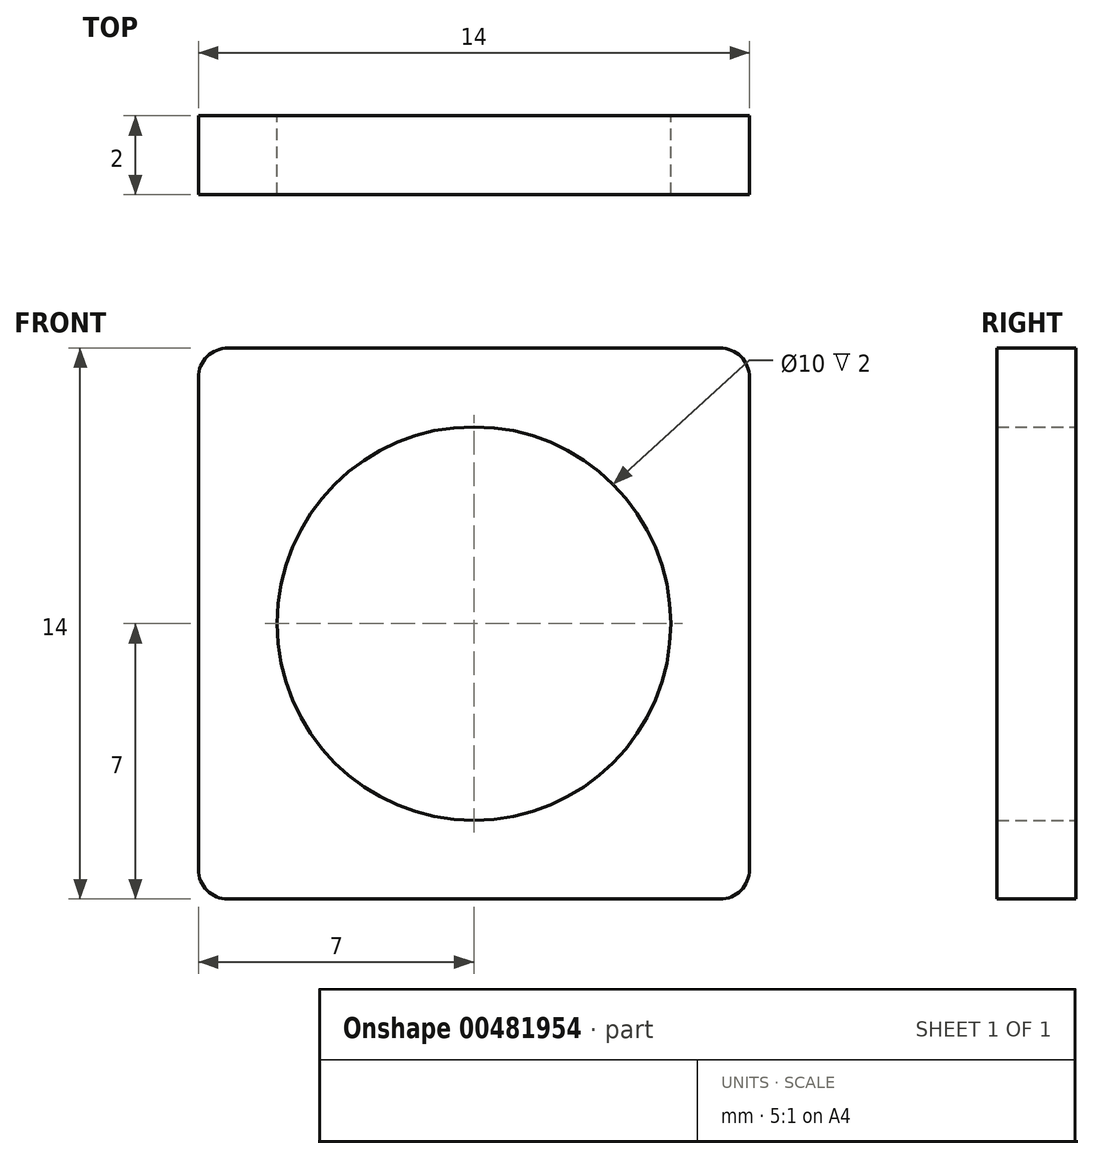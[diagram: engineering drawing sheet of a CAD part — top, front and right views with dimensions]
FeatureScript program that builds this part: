
annotation { "Feature Type Name" : "Feature", "Feature Type Description" : "" }
export const myFeature = defineFeature(function(context is Context, id is Id, definition is map)
    precondition{}
    {
        {
            var Q0;
            Q0=qCreatedBy(makeId("Front.planeOp"),FACE);
            var sketch = newSketch(context, id + "F0", { "sketchPlane" : qUnion([Q0])});
            skLineSegment(sketch, "E0.bottom", {"start": v(-6.25, 7) * mm, "end": v(6.25, 7) * mm});
            skLineSegment(sketch, "E0.top", {"start": v(-6.25, -7) * mm, "end": v(6.25, -7) * mm});
            skLineSegment(sketch, "E0.left", {"start": v(-7, 6.25) * mm, "end": v(-7, -6.25) * mm});
            skLineSegment(sketch, "E0.right", {"start": v(7, 6.25) * mm, "end": v(7, -6.25) * mm});
            skPoint(sketch, "E0.middle", {"position": v(0, 0) * mm});
            skCircle(sketch, "E1", {"center": v(0, 0) * mm, "radius": 5 * mm});
            skPoint(sketch, "E2.visualSharp", {"position": v(-7, 7) * mm});
            skArc(sketch, "E2.filletArc", {"start": v(-6.25, 7) * mm, "mid": v(-6.78, 6.78) * mm, "end": v(-7, 6.25) * mm});
            skPoint(sketch, "E3.visualSharp", {"position": v(-7, -7) * mm});
            skArc(sketch, "E3.filletArc", {"start": v(-7, -6.25) * mm, "mid": v(-6.78, -6.78) * mm, "end": v(-6.25, -7) * mm});
            skPoint(sketch, "E4.visualSharp", {"position": v(7, -7) * mm});
            skArc(sketch, "E4.filletArc", {"start": v(6.25, -7) * mm, "mid": v(6.78, -6.78) * mm, "end": v(7, -6.25) * mm});
            skPoint(sketch, "E5.visualSharp", {"position": v(7, 7) * mm});
            skArc(sketch, "E5.filletArc", {"start": v(7, 6.25) * mm, "mid": v(6.78, 6.78) * mm, "end": v(6.25, 7) * mm});
            skSolve(sketch);
        }
        {
            var Q0;
            Q0 = qSketchRegion(id + "F0", true);
            extrude(context, id + "F1", {"entities" : qUnion([Q0]), "depth" : 2 * mm});
        }
    });
